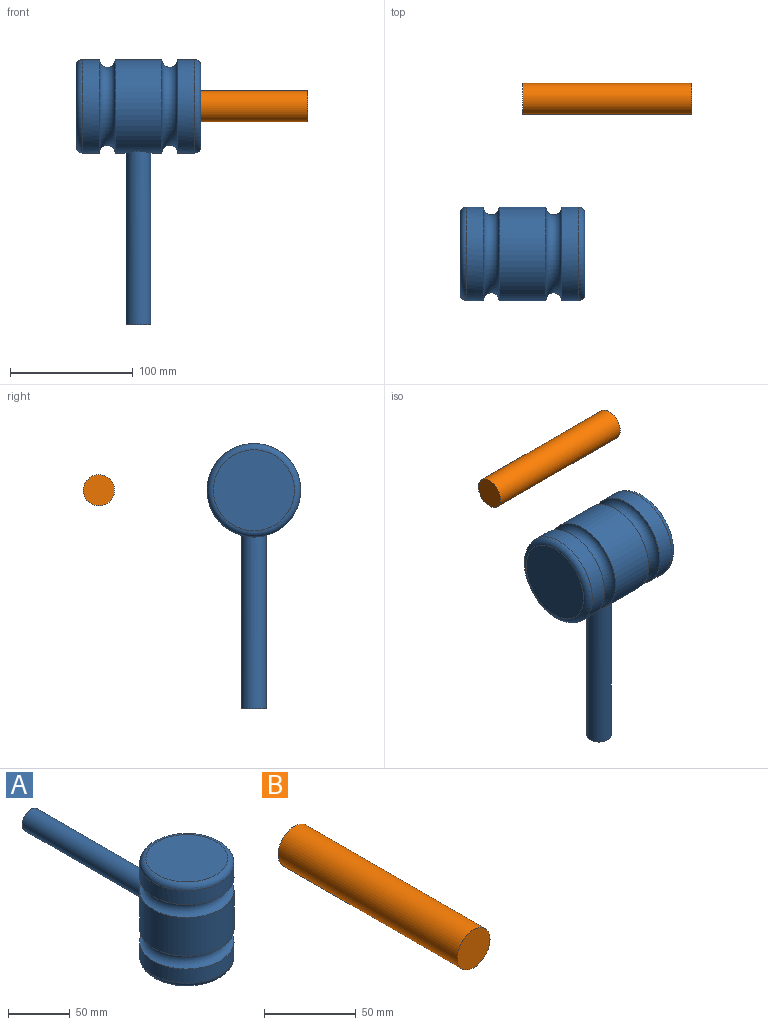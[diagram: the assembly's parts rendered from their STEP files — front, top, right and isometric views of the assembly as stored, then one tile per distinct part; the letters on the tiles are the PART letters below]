
ASSEMBLY  parts=2 mates=1
PART A: 11 faces, bbox 92.2x223.9x101.6 mm
  f0: torus R=38.1mm, axis (0,0,-1), area 4268.9mm2, adj f1,f6
  f1: cylinder r=38.1mm len=76.2mm, axis (0,0,-1), area 3344.3mm2, adj f0,f7
  f2: plane 66.04x66.04mm, normal (0,0,1), area 3425.3mm2, adj f7
  f3: plane 66.04x66.04mm, normal (0,0,-1), area 3425.3mm2, adj f8
  f4: cylinder r=38.1mm len=76.2mm, axis (0,0,-1), area 3344.3mm2, adj f5,f8
  f5: torus R=38.1mm, axis (0,0,-1), area 4268.9mm2, adj f4,f6
  f6: cylinder r=38.1mm len=76.2mm, axis (0,0,-1), area 8793.7mm2, adj f0,f5,f9
  f7: torus R=33.02mm, axis (0,0,1), area 1817.7mm2, adj f1,f2
  f8: torus R=33.02mm, axis (0,0,1), area 1817.7mm2, adj f3,f4
  f9: cylinder r=10.16mm len=141.08mm, axis (0,-1,0), area 8961.9mm2, adj f6,f10
  f10: plane 20.32x20.32mm, normal (0,1,0), area 324.3mm2, adj f9
PART B: 3 faces, bbox 25.4x137.9x25.4 mm
  f0: cylinder r=12.7mm len=137.92mm, axis (0,1,0), area 11005.7mm2, adj f1,f2
  f1: plane 25.4x25.4mm, normal (0,-1,0), area 506.7mm2, adj f0
  f2: plane 25.4x25.4mm, normal (0,1,0), area 506.7mm2, adj f0
PLACE A rot(axis=(-0.58,0.58,-0.58),120deg) t=(-185.55,-11.92,85.13)mm
PLACE B rot(axis=(0,0,-1),90deg) t=(3.17,152.46,85.13)mm
MATE planar A.f8 <-> B.f0  axis (-1,0,0) through (-134.75,26.18,85.13)mm
